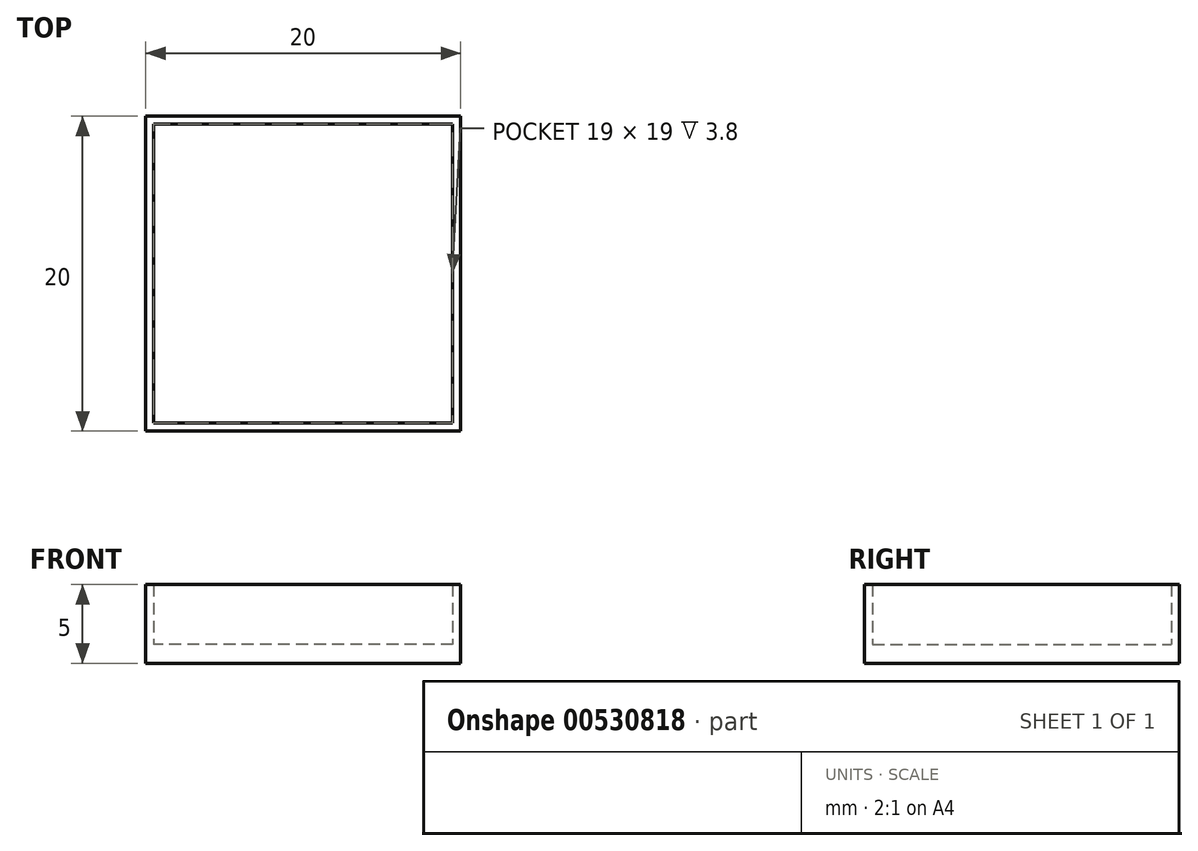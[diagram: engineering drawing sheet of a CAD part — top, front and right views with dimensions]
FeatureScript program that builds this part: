
annotation { "Feature Type Name" : "Feature", "Feature Type Description" : "" }
export const myFeature = defineFeature(function(context is Context, id is Id, definition is map)
    precondition{}
    {
        {
            var Q0;
            Q0=qCreatedBy(makeId("Top.planeOp"),FACE);
            var sketch = newSketch(context, id + "F0", { "sketchPlane" : qUnion([Q0])});
            skLineSegment(sketch, "E0.bottom", {"start": v(10, -10) * mm, "end": v(-10, -10) * mm});
            skLineSegment(sketch, "E0.top", {"start": v(10, 10) * mm, "end": v(-10, 10) * mm});
            skLineSegment(sketch, "E0.left", {"start": v(10, -10) * mm, "end": v(10, 10) * mm});
            skLineSegment(sketch, "E0.right", {"start": v(-10, -10) * mm, "end": v(-10, 10) * mm});
            skPoint(sketch, "E0.middle", {"position": v(0, 0) * mm});
            skSolve(sketch);
        }
        {
            var Q0;
            Q0 = qSketchRegion(id + "F0", true);
            extrude(context, id + "F1", {"entities" : qUnion([Q0]), "depth" : 5 * mm, "offsetDistance" : 25 * mm});
        }
        {
            var Q0;
            Q0=makeQuery(id+"F1.opExtrude","CAP_FACE",FACE,{"disambiguationData":[OSD([sQuery(id+"F0.wireOp",EDGE,"E0.bottom"),sQuery(id+"F0.wireOp",EDGE,"E0.top"),sQuery(id+"F0.wireOp",EDGE,"E0.left"),sQuery(id+"F0.wireOp",EDGE,"E0.right")])],"isStart":false});
            var Q1;
            Q1=makeQuery(id+"F1.opExtrude","CAP_FACE",FACE,{"disambiguationData":[OSD([sQuery(id+"F0.wireOp",EDGE,"E0.bottom"),sQuery(id+"F0.wireOp",EDGE,"E0.top"),sQuery(id+"F0.wireOp",EDGE,"E0.left"),sQuery(id+"F0.wireOp",EDGE,"E0.right")])],"isStart":true});
            shell(context, id + "F2", {"entities" : qUnion([Q0, Q1]), "thickness" : 0.5 * mm});
        }
        {
            var Q0;
            Q0=qCreatedBy(makeId("Top.planeOp"),FACE);
            var sketch = newSketch(context, id + "F3", { "sketchPlane" : qUnion([Q0])});
            skLineSegment(sketch, "E1.0", {"start": v(-10, -10) * mm, "end": v(-10, 10) * mm});
            skLineSegment(sketch, "E2.0", {"start": v(10, 10) * mm, "end": v(-10, 10) * mm});
            skLineSegment(sketch, "E3.0", {"start": v(10, -10) * mm, "end": v(10, 10) * mm});
            skLineSegment(sketch, "E4.0", {"start": v(10, -10) * mm, "end": v(-10, -10) * mm});
            skSolve(sketch);
        }
        {
            var Q0;
            Q0 = qSketchRegion(id + "F3", true);
            extrude(context, id + "F4", {"entities" : qUnion([Q0]), "operationType" : NewBodyOperationType.ADD, "depth" : 1.2 * mm, "offsetDistance" : 25 * mm});
        }
    });
